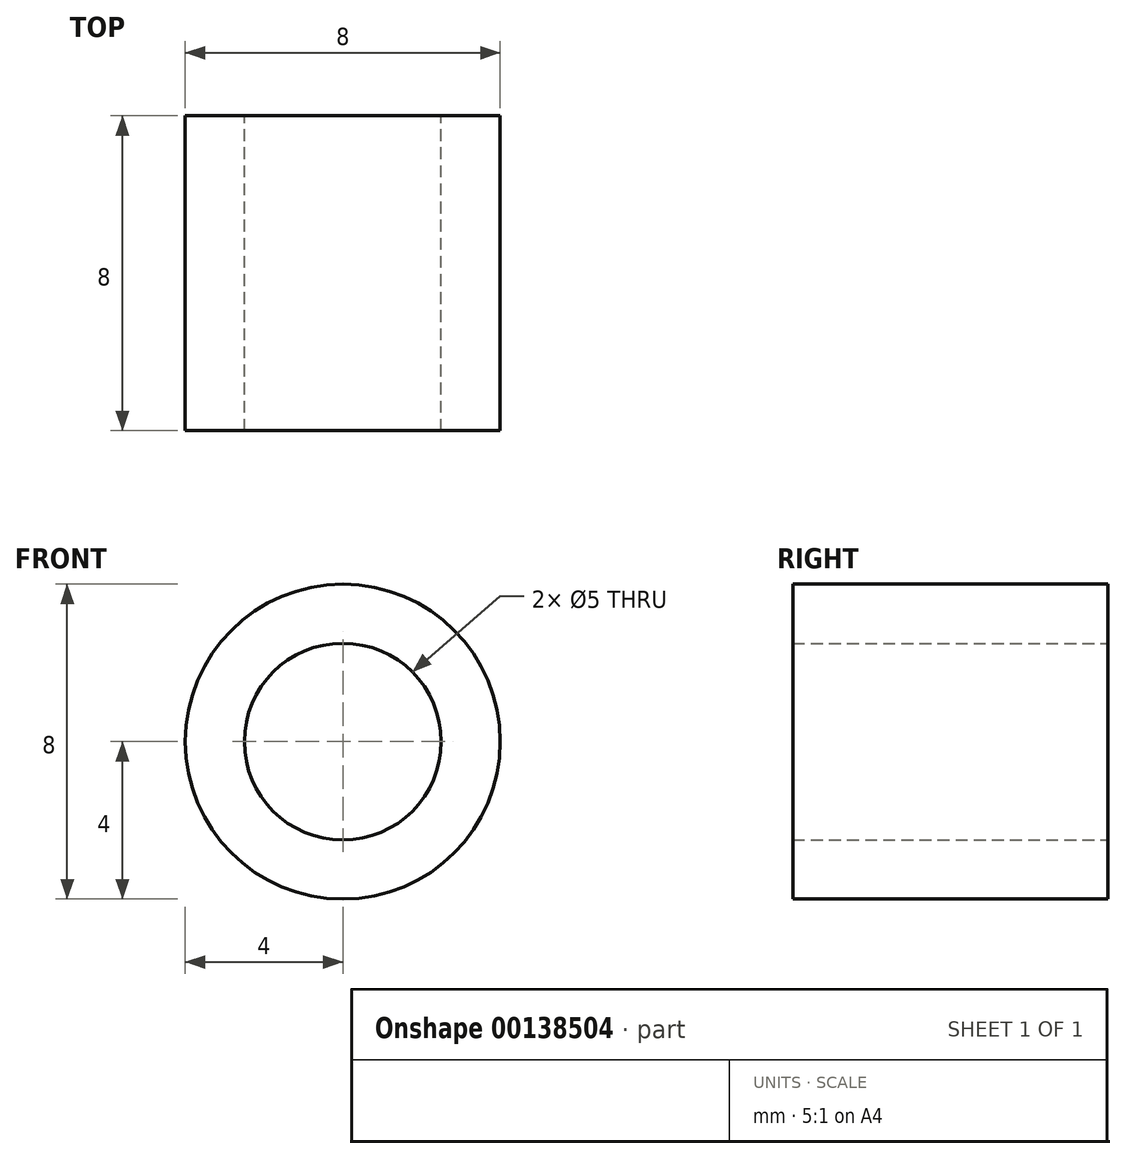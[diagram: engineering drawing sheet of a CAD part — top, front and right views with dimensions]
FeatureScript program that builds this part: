
annotation { "Feature Type Name" : "Feature", "Feature Type Description" : "" }
export const myFeature = defineFeature(function(context is Context, id is Id, definition is map)
    precondition{}
    {
        {
            var Q0;
            Q0=qCreatedBy(makeId("Front.planeOp"),FACE);
            var sketch = newSketch(context, id + "F0", { "sketchPlane" : qUnion([Q0])});
            skCircle(sketch, "E0", {"center": v(0, 0) * mm, "radius": 2.5 * mm});
            skCircle(sketch, "E1", {"center": v(0, 0) * mm, "radius": 4 * mm});
            skSolve(sketch);
        }
        {
            var Q0;
            Q0=makeQuery(id+"F0.imprint","IMPRINT",FACE,{"disambiguationData":[TD([[makeQuery(id+"F0.imprint","IMPRINT",EDGE,{"derivedFrom":sQuery(id+"F0.wireOp",EDGE,"E0")}),-1.0]])]});
            var Q1;
            Q1=makeQuery(id+"F0.imprint","IMPRINT",FACE,{"disambiguationData":[TD([[makeQuery(id+"F0.imprint","IMPRINT",EDGE,{"derivedFrom":sQuery(id+"F0.wireOp",EDGE,"E0")}),-1.0]])]});
            extrude(context, id + "F1", {"entities" : qUnion([Q0, Q1]), "depth" : 8 * mm});
        }
    });
